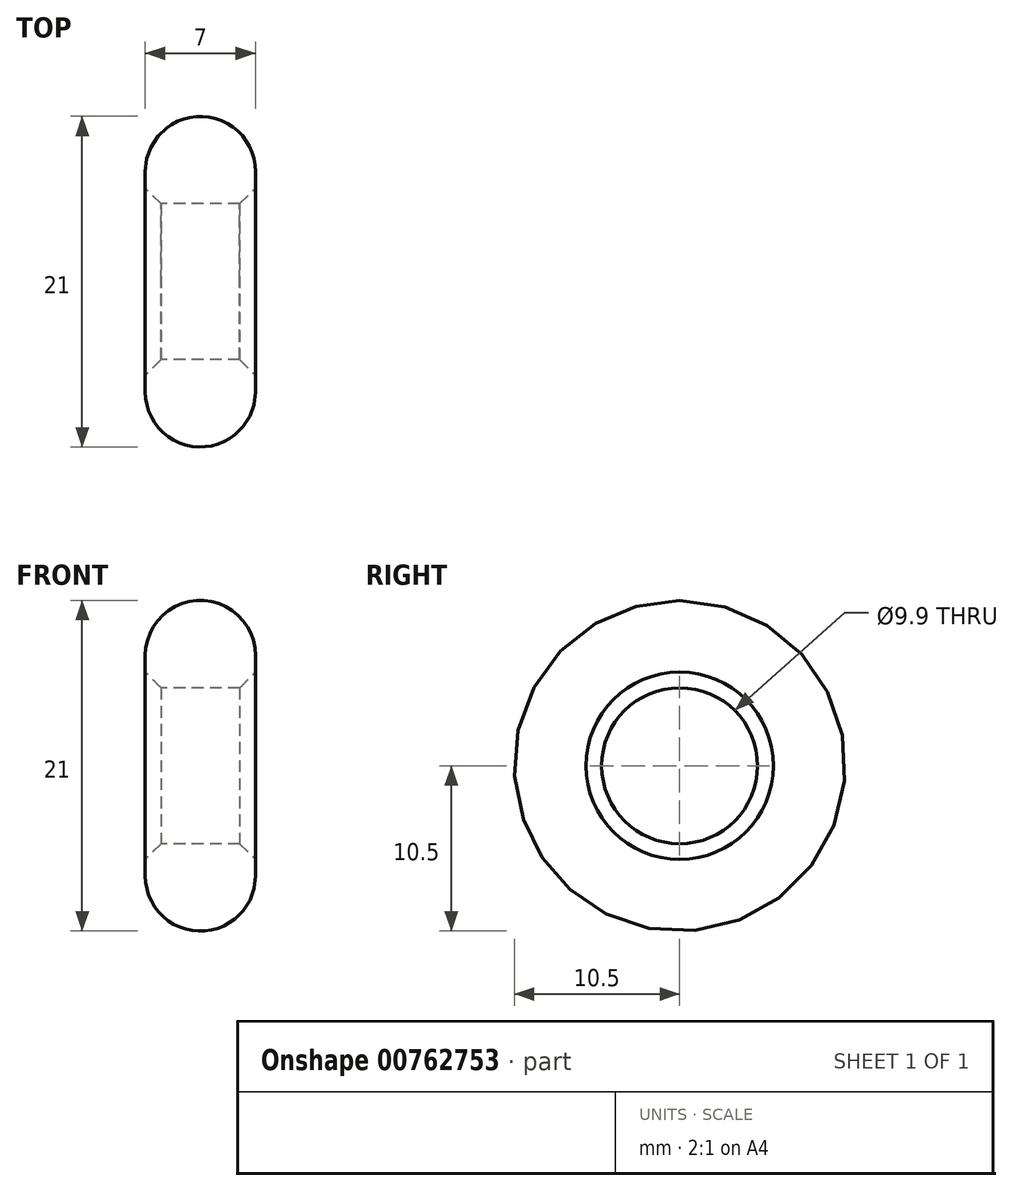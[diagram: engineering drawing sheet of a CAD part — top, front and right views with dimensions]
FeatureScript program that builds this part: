
annotation { "Feature Type Name" : "Feature", "Feature Type Description" : "" }
export const myFeature = defineFeature(function(context is Context, id is Id, definition is map)
    precondition{}
    {
        {
            var Q0;
            Q0=qCreatedBy(makeId("Front.planeOp"),FACE);
            var sketch = newSketch(context, id + "F0", { "sketchPlane" : qUnion([Q0])});
            skLineSegment(sketch, "E0", {"start": v(-3.5, 0) * mm, "end": v(3.5, 0) * mm, "construction": true});
            skLineSegment(sketch, "E1", {"start": v(-3.5, 0) * mm, "end": v(-3.5, 7) * mm});
            skLineSegment(sketch, "E2", {"start": v(3.5, 0) * mm, "end": v(3.5, 7) * mm});
            skLineSegment(sketch, "E3", {"start": v(-3.5, 4.95) * mm, "end": v(3.5, 4.95) * mm});
            skArc(sketch, "E4", {"start": v(3.5, 7) * mm, "mid": v(0, 10.5) * mm, "end": v(-3.5, 7) * mm});
            skLineSegment(sketch, "E5", {"start": v(0, 10.5) * mm, "end": v(0, 0) * mm, "construction": true});
            skSolve(sketch);
        }
        {
            var Q0;
            {var subQ2=sQuery(id+"F0.wireOp",EDGE,"E3");Q0=makeQuery(id+"F0.imprint","IMPRINT",FACE,{"disambiguationData":[TD([[makeQuery(id+"F0.imprint","IMPRINT",EDGE,{"derivedFrom":subQ2}),1.0]])]});}
            var Q1;
            Q1=sQuery(id+"F0.wireOp",EDGE,"E0");
            revolve(context, id + "F1", {"surfaceOperationType" : NewSurfaceOperationType.NEW, "entities" : qUnion([Q0]), "axis" : qUnion([Q1]), "revolveType" : RevolveType.FULL});
        }
        {
            var Q0;
            Q0=makeQuery(id+"F1.opRevolve","SWEPT_EDGE",EDGE,{"disambiguationData":[OSD([sQuery(id+"F0.wireOp",EDGE,"E2"),sQuery(id+"F0.wireOp",EDGE,"E3")])]});
            var Q1;
            Q1=makeQuery(id+"F1.opRevolve","SWEPT_EDGE",EDGE,{"disambiguationData":[OSD([sQuery(id+"F0.wireOp",EDGE,"E1"),sQuery(id+"F0.wireOp",EDGE,"E3")])]});
            chamfer(context, id + "F2", {"entities" : qUnion([Q0, Q1]), "width" : 1 * mm, "tangentPropagation" : true});
        }
    });
